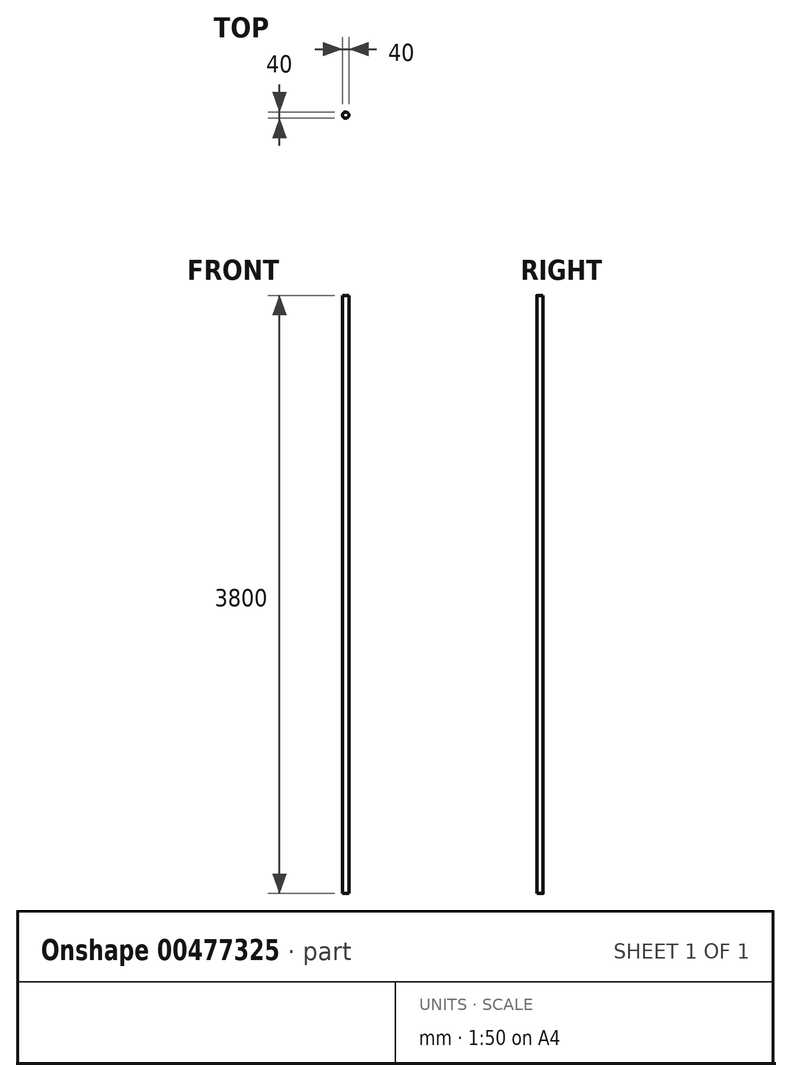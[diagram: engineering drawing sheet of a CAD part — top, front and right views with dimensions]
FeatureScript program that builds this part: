
annotation { "Feature Type Name" : "Feature", "Feature Type Description" : "" }
export const myFeature = defineFeature(function(context is Context, id is Id, definition is map)
    precondition{}
    {
        {
            var Q0;
            Q0=qCreatedBy(makeId("Top.planeOp"),FACE);
            var sketch = newSketch(context, id + "F0", { "sketchPlane" : qUnion([Q0])});
            skCircle(sketch, "E0", {"center": v(0, 0) * mm, "radius": 20 * mm});
            skSolve(sketch);
        }
        {
            var Q0;
            Q0 = qSketchRegion(id + "F0", true);
            extrude(context, id + "F1", {"entities" : qUnion([Q0]), "depth" : 3800 * mm});
        }
    });
